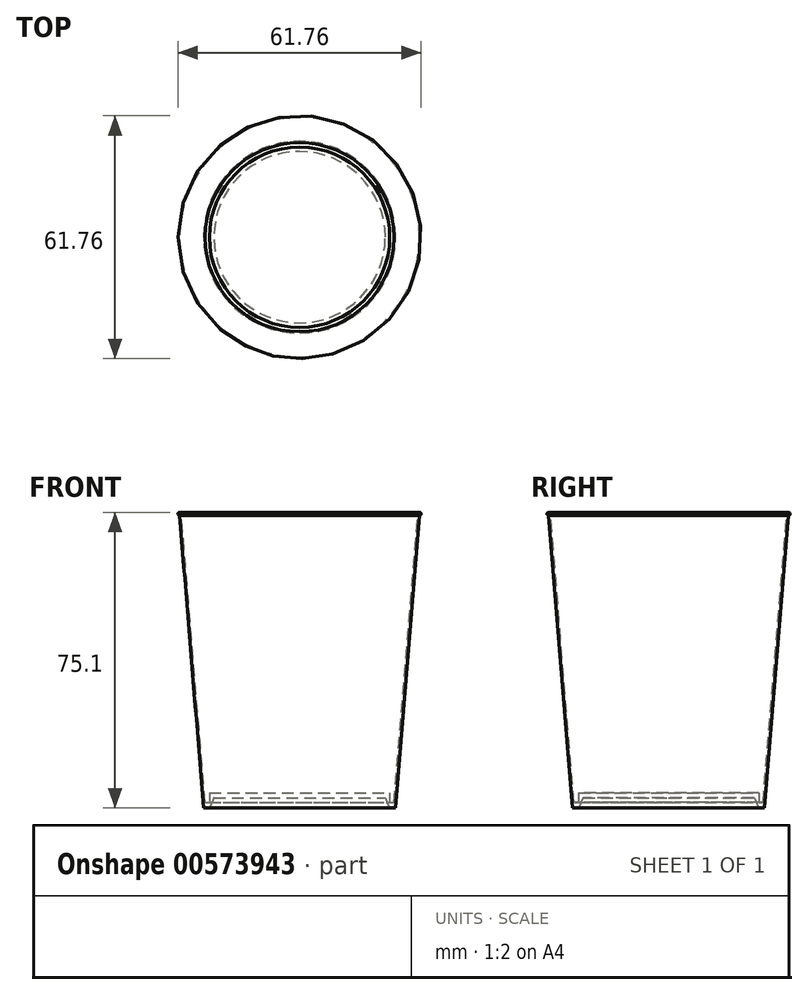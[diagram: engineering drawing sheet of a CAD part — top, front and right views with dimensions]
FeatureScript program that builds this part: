
annotation { "Feature Type Name" : "Feature", "Feature Type Description" : "" }
export const myFeature = defineFeature(function(context is Context, id is Id, definition is map)
    precondition{}
    {
        {
            var Q0;
            Q0=qCreatedBy(makeId("Front.planeOp"),FACE);
            var sketch = newSketch(context, id + "F0", { "sketchPlane" : qUnion([Q0])});
            skLineSegment(sketch, "E0", {"start": v(0, 2.48) * mm, "end": v(-22.9, 2.48) * mm});
            skLineSegment(sketch, "E1", {"start": v(-22.9, 2.48) * mm, "end": v(-22.9, 0) * mm});
            skLineSegment(sketch, "E2", {"start": v(-22.9, 0) * mm, "end": v(-24.02, 0) * mm});
            skLineSegment(sketch, "E3", {"start": v(-24.02, 0) * mm, "end": v(-30.06, 73.4) * mm});
            skArc(sketch, "E4", {"start": v(-30.06, 73.4) * mm, "mid": v(-30.76, 73.64) * mm, "end": v(-30.48, 72.95) * mm});
            skLineSegment(sketch, "E5", {"start": v(-30.48, 72.95) * mm, "end": v(-24.38, -1.33) * mm});
            skLineSegment(sketch, "E6", {"start": v(-24.38, -1.33) * mm, "end": v(-22.78, -1.2) * mm});
            skLineSegment(sketch, "E7", {"start": v(-22.78, -1.2) * mm, "end": v(-21.77, 1.24) * mm});
            skPoint(sketch, "E7.endSnap0", {"position": v(-22.9, 1.24) * mm});
            skLineSegment(sketch, "E8", {"start": v(-21.77, 1.24) * mm, "end": v(0, 1.24) * mm});
            skLineSegment(sketch, "E9", {"start": v(0, 1.24) * mm, "end": v(0, 2.48) * mm});
            skSolve(sketch);
        }
        {
            var Q0;
            Q0=makeQuery(id+"F0.imprint","IMPRINT",FACE,{"disambiguationData":[TD([[makeQuery(id+"F0.imprint","IMPRINT",EDGE,{"derivedFrom":sQuery(id+"F0.wireOp",EDGE,"E0")}),1.0]])]});
            var Q1;
            Q1=sQuery(id+"F0.wireOp",EDGE,"E9");
            revolve(context, id + "F1", {"entities" : qUnion([Q0]), "axis" : qUnion([Q1]), "revolveType" : RevolveType.FULL});
        }
    });
